# Revit family: Gira_216700
name_source: partatom
category: Elektroinstallationen
revit_build: Autodesk Revit 2017 (Build: 20160225_1515(x64)
units: mm (PartAtom-declared; Revit-internal decimal feet)

## family parameters
Basisbauteil = Fläche
Beim Laden mit Abzugskörper schneiden = Nein
Bemaßung runder Anschluss = Durchmesser verwenden
Beschriftungsausrichtung beibehalten = Nein
Gemeinsam genutzt = Nein
Raumberechnungspunkt = Nein
Teiletyp = Normal

## types (1)
- KNX IP-Router KNX REG
    Anzahl der Eingänge = 0
    BIM = https://media.stage.bim.site X1 REG KNX.rfa
    BIMSITE_PRODUCT_ID = ae5a2d61a97159a84ca3a2909b559f3bdc49fc3b
    Beschreibung = KNX IP-Router  REG plus Merkmale:  Verbindung von KNX Linien mit Hilfe von Datennetzwerken unter Nutzung des Internet Protokolls (IP).  Ankopplung an ein KNX System zusammen mit dem Gira HomeServer bzw. Gira FacilityServer.  Filtern und Weiterleiten von Telegrammen.  Einsatz als Linien- oder Bereichskoppler.  Verwendung als KNX Zeitgeber.  Aufzeichnen von KNX Telegrammen auf microSD-Karte.  KNX Data Secure und KNX IP Secure zur sicheren und manipulationsgeschützten Kommunikation im KNX.  Bis zu vier Tunneling-Verbindungen gleichzeitig möglich.  Zuverlässige Kommunikation zur automatischen Korrektur von Telegrammverlusten im WLAN (Reliable Communication).  Hinweise :  Versorgung über externe DC 24 V.  Für Firmware-Updates wird der Gira Projekt Assistent (GPA) benötigt. Der GPA ist kostenlos im Gira Downloadbereich verfügbar.
    Breite in Teilungseinheiten = 0
    Bussystem Funkbus = Nein
    Bussystem KNX = Nein
    Bussystem KNX-Funk = Nein
    Bussystem LON = Nein
    Bussystem Powernet = Nein
    Datenblatt = https://media.stage.bim.site
    Datenblatt 1 = https://media.stage.bim.site
    Funktion Schalten = Nein
    GTIN = 4010337084440
    HAN = 216700
    HeinzeBIM = https://www.heinze.de
    Hersteller = Gira
    Kosten = 0 $
    Max. Anzahl der Jalousieausgänge = 0
    Max. Schaltleistung [Voltampere] = 0
    Mit Busankopplung = Nein
    Mit LED-Anzeige = Nein
    Produktseite = https://media.stage.bim.site
    Typname = KNX IP-Router KNX REG
    URL = https://www.gira.de
    Vor Ort-/Handbedienung = Nein
    Vorgabe-Ansicht = 1219 mm

## geometry (parser evidence)
native form markers: Sweep x2
no freeform markers — native parametric forms only
